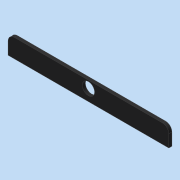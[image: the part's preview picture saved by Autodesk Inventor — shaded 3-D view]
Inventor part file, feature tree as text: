
AUTODESK INVENTOR PART (.ipt)
format: ipt  version: 2020 (Build 240168000, 168)  size: 89,088 bytes
history: native  units: mm
features: other x1, extrude x1, fillet x1
ambient origin geometry x8: Origin, YZ Plane, XZ Plane, XY Plane, X Axis, Y Axis, Z Axis, Center Point
bodies: Body1 (feature_tree)
feature tree (3):
  other  "實體1"
  extrude  "擠出1"  Depth=15.0mm
  fillet  "圓角1"  Radius=130.0mm
